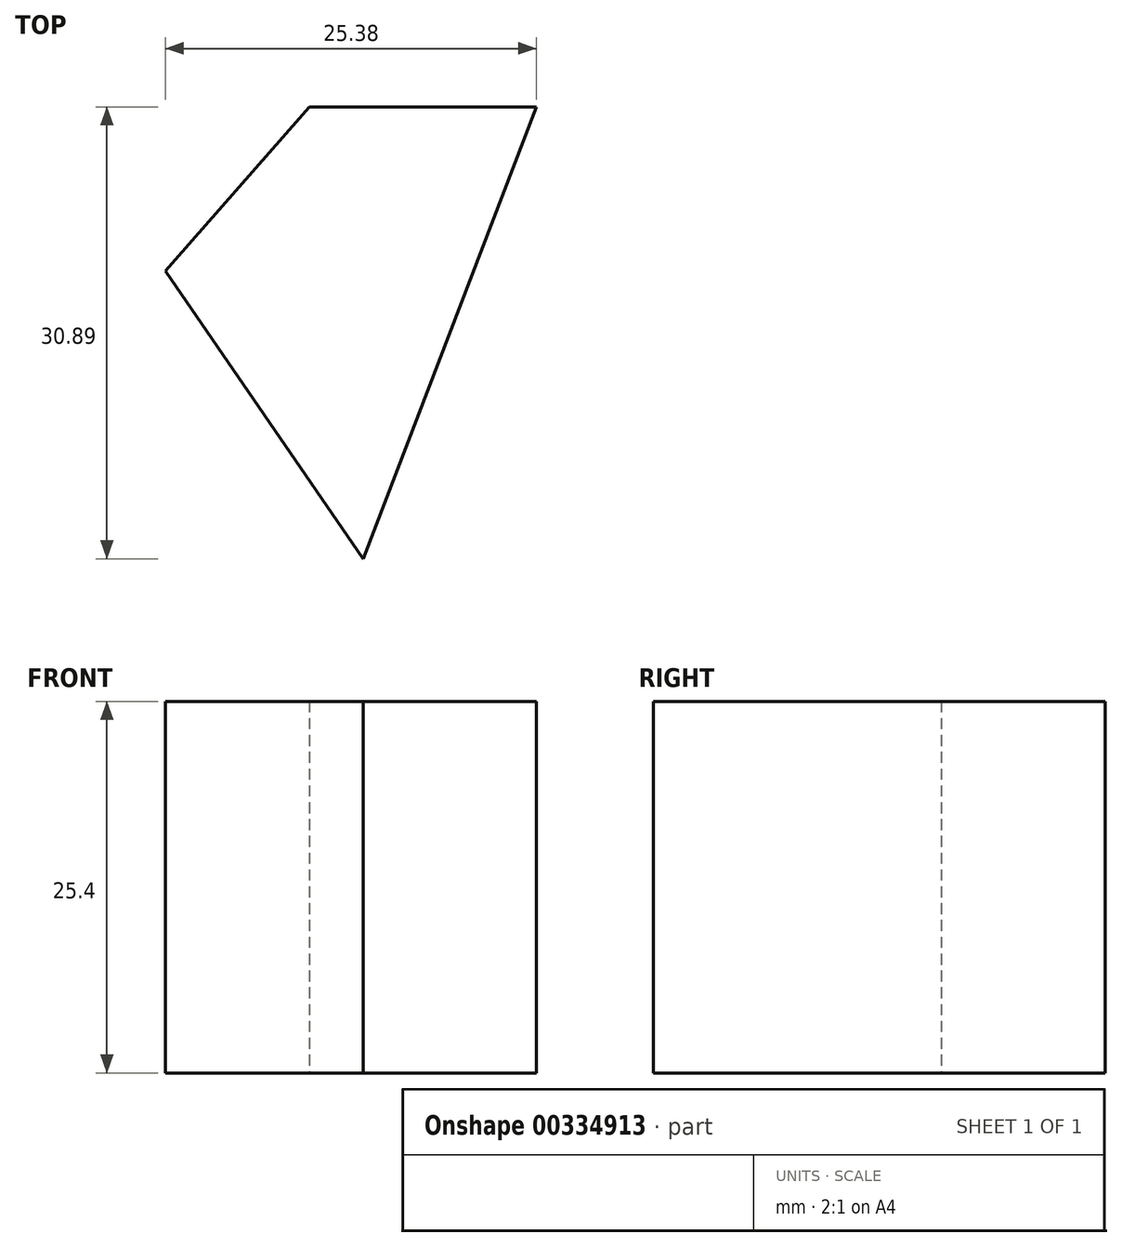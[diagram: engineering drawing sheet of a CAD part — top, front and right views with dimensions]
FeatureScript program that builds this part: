
annotation { "Feature Type Name" : "Feature", "Feature Type Description" : "" }
export const myFeature = defineFeature(function(context is Context, id is Id, definition is map)
    precondition{}
    {
        {
            var Q0;
            Q0=qCreatedBy(makeId("Top.planeOp"),FACE);
            var sketch = newSketch(context, id + "F0", { "sketchPlane" : qUnion([Q0])});
            skLineSegment(sketch, "E0", {"start": v(-74.5, 0) * mm, "end": v(-64.67, 11.23) * mm});
            skLineSegment(sketch, "E1", {"start": v(-64.67, 11.23) * mm, "end": v(-49.12, 11.23) * mm});
            skLineSegment(sketch, "E2", {"start": v(-49.12, 11.23) * mm, "end": v(-60.98, -19.66) * mm});
            skLineSegment(sketch, "E3", {"start": v(-60.98, -19.66) * mm, "end": v(-74.5, 0) * mm});
            skLineSegment(sketch, "E4", {"start": v(-65.06, 56.3) * mm, "end": v(-69.59, 5.62) * mm});
            skLineSegment(sketch, "E5", {"start": v(-69.59, 5.62) * mm, "end": v(-63.37, -1.54) * mm});
            skSolve(sketch);
        }
        {
            var Q0;
            {var subQ0=sQuery(id+"F0.wireOp",EDGE,"E1");Q0=makeQuery(id+"F0.imprint","IMPRINT",FACE,{"disambiguationData":[TD([[makeQuery(id+"F0.imprint","IMPRINT",EDGE,{"derivedFrom":subQ0}),-1.0]])]});}
            extrude(context, id + "F1", {"entities" : qUnion([Q0]), "depth" : 25.4 * mm});
        }
    });
